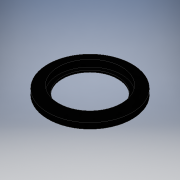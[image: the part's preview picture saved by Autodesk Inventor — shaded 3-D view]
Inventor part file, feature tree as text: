
AUTODESK INVENTOR PART (.ipt)
format: ipt  version: 2016 (Build 200138000, 138)  size: 110,080 bytes
history: native  units: in
note: dims shown in document units (in); Inventor stores cm internally (conversion verified against a paired STEP export)
features: revolve x1, sketch x1
ambient origin geometry x8: Origin, YZ Plane, XZ Plane, XY Plane, X Axis, Y Axis, Z Axis, Center Point
bodies: Solid1 (feature_tree)
feature tree (2):
  revolve  "Revolution1"  [1 undecoded]
  sketch  "Sketch1"  dims[d0=0.8265in d1=0.175in d2=0.05in d3=0.1in d4=0.15in d5=0.275in d6=90.0deg]
note: 1 required parameter value undecoded (feature->parameter linkage not recoverable at this tier; creation-order binding heuristic only, values carry confidence <= 0.55)
